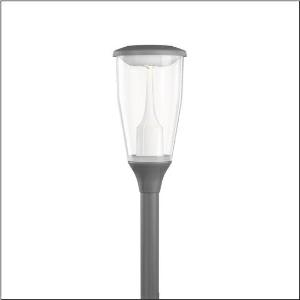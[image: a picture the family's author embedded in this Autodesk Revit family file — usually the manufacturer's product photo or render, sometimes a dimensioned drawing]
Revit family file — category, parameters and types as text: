
# Revit family: dl_11_iq___st1_2a_5xa5565ef14h000022_473d
name_source: partatom
category: Lighting Fixtures
units: mm (PartAtom-declared; Revit-internal decimal feet)

## family parameters
Cut with Voids When Loaded = No
Host = Face
Light Source = No
Part Type = Normal
Room Calculation Point = No
Round Connector Dimension = Use Diameter
Shared = No

## types (1)
- --- (1 x LED, 1560 lm, 10.5 W, 3000K)
    Apparent Load = 11 VA
    CIE Flux Codes = 24 63 94 96 100
    Color Rendering = 70
    Color Temperature = 3000K
    Default Elevation = 1800 mm
    Description = DL 11 iQ, mast luminaire, Module 540 iQ-SR, primary light control with 3 zone facetted reflector, of plastic, silver coated, highly specular, structured, primary optical cover: cover, of PMMA, transparent, light distribution: ST1.2a, light emission: direct distribution, primary light characteristic: asymmetric, installation type: post-top, LED, High Power LED, rated luminous flux: 1.560lm, luminous efficacy: 149lm/W, light colour: 730, colour temperature: 3000K, control: Street-Remote, Auto-Match, Temp-Guard, Lumen-Switch, Night-Set, Smart-Wire, Light-Fading, Desk-Remote (wireless, voltage-free reading and setting of iQ features in the workshop via application-optimized NFC function/RFID function), optimised constant luminous flux control (CLO 2.0), mains connection: 220..240V, AC, 50/60Hz, connection cable pre-assembled, cable length: 5,5m, start of lifetime: 10W, end of service life: 11W, reduction: 5W, luminaire housing, upper part, of diecast aluminium, coated, Siteco® metallic grey (DB 702S), spigot size: 60mm (post-top), post-top mast mounting element, of diecast aluminium, coated, Siteco® metallic grey (DB 702S), Module 540 iQ-SR, traffic white (RAL 9016), equipment: standard, protection rating (complete): IP66, insulation class (complete): insulation class II (safety insulation), certification: CE, ENEC, ENEC+, VDE, packaging unit: 1 piece

Light Distribution: ST1.2a
    Height = 665 mm
    Lamp = 1 x LED
    Lamp Light Flux = 1560 lm
    Lamp Power = 10.5 W
    Lamp count = 1
    Length = 334 mm
    Luminous efficacy = 149 lm/W
    Manufacturer = Siteco
    ModVariant = No
    Model = 5XA5565EF14H000022
    Number of Poles = 1
    OnlyDefault = Yes
    Power Factor = 1
    Product Name = DL 11 iQ | ST1.2a
    Product group = mast luminaire | pylon top
    ProductGroupID = 6100
    Protection Class = Protection class II
    Protection Degree = IP 66
    RLX_Detail_Level = 1
    RLX_Emergency_Light_Flux = 0 lm
    RLX_Emergency_Type = 0
    RLX_Emergency_Type_DB = No
    RlxData = <blob elided: 152737 chars, md5=95e8e66e>
    Socket = socket
    Standby Power = 0 W
    System Light Flux = 1560 lm
    System Power = 11 W
    Type Comments = factory setting: luminous flux: 100 % | dim-lin: 254 | 419 mA
    Type Image = l_1258354.jpg
    URL = http://relux.com
    VarID = @adj_044061
    Voltage = 0 V
    Weight = 0.00 kg
    Width = 0 mm  [stored 0 ft]

note: [stored X ft] marks values corroborated as IEEE doubles in the binary element streams (Revit-internal decimal feet)

## geometry (parser evidence)
native form markers: Blend x4, Sweep x9
no freeform markers — native parametric forms only
